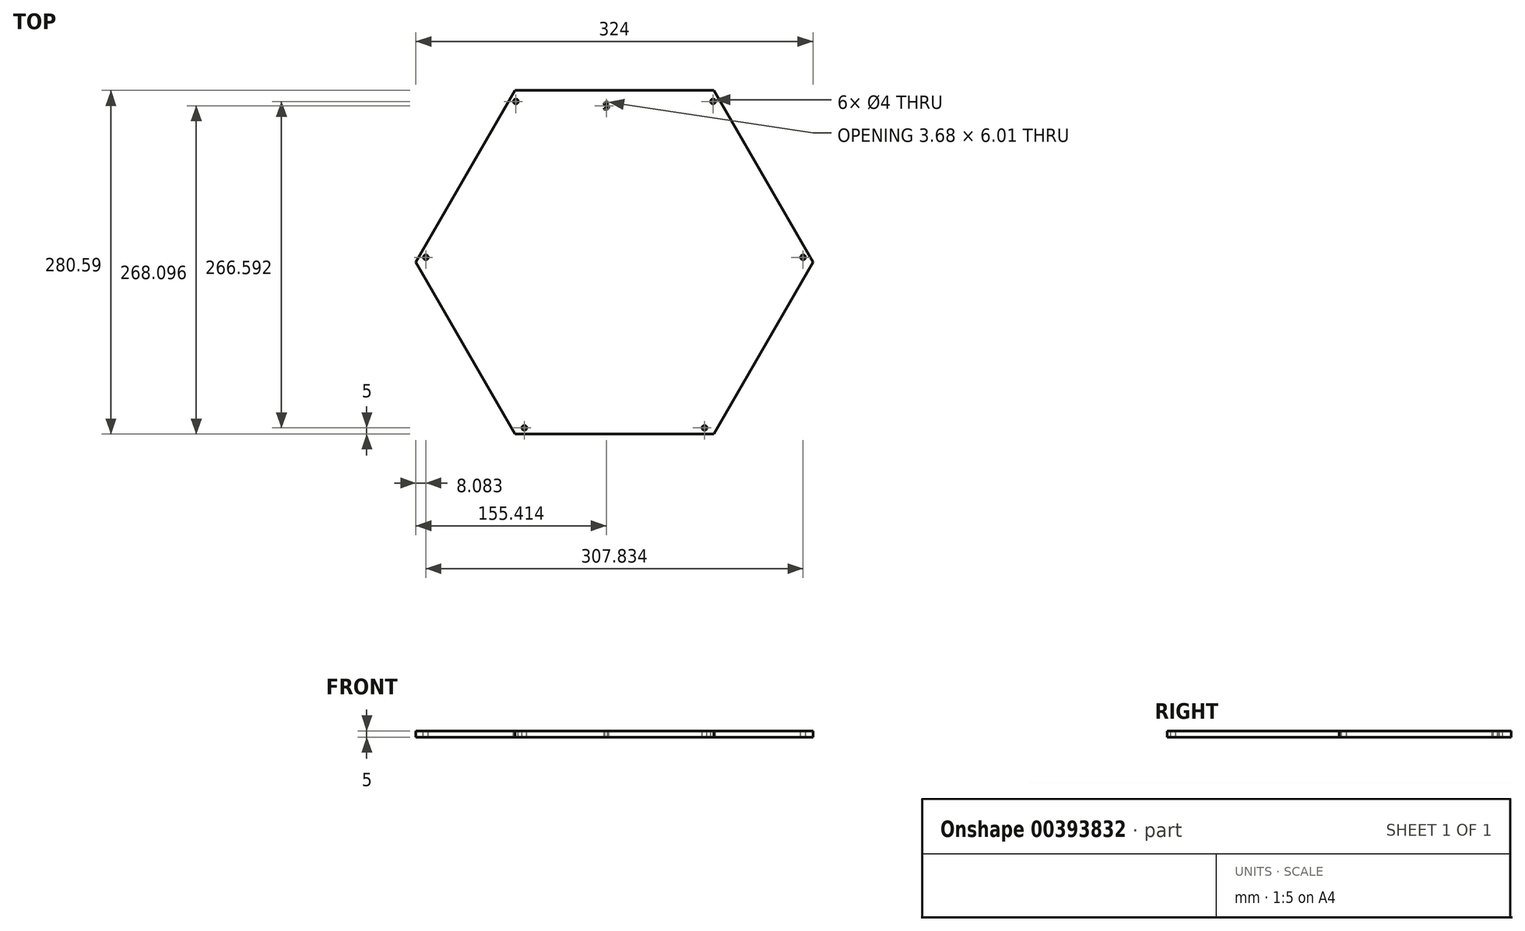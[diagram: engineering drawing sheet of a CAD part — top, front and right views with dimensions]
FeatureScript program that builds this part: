
annotation { "Feature Type Name" : "Feature", "Feature Type Description" : "" }
export const myFeature = defineFeature(function(context is Context, id is Id, definition is map)
    precondition{}
    {
        {
            var Q0;
            Q0=qCreatedBy(makeId("Top.planeOp"),FACE);
            var sketch = newSketch(context, id + "F0", { "sketchPlane" : qUnion([Q0])});
            skLineSegment(sketch, "E0", {"start": v(-81, 0) * mm, "end": v(81, 0) * mm});
            skLineSegment(sketch, "E1", {"start": v(-81, 280.6) * mm, "end": v(-162, 140.3) * mm});
            skCircle(sketch, "E2", {"center": v(0, 140.3) * mm, "radius": 140.3 * mm, "construction": true});
            skLineSegment(sketch, "E3.0", {"start": v(-81, 280.6) * mm, "end": v(81, 280.6) * mm});
            skLineSegment(sketch, "E3.2", {"start": v(162, 140.3) * mm, "end": v(81, 0) * mm});
            skLineSegment(sketch, "E3.4", {"start": v(-81, 0) * mm, "end": v(-162, 140.3) * mm});
            skPoint(sketch, "E3.0.midPoint", {"position": v(0, 280.6) * mm});
            skPoint(sketch, "E4.orphan", {"position": v(0, 420.89) * mm});
            skPoint(sketch, "E5.orphan", {"position": v(-243, 0) * mm});
            skPoint(sketch, "E6.orphan", {"position": v(243, 0) * mm});
            skLineSegment(sketch, "E7", {"start": v(81, 280.6) * mm, "end": v(162, 140.3) * mm});
            skSolve(sketch);
        }
        {
            var Q0;
            Q0=qSketchRegion(id+"F0",true);
            extrude(context, id + "F1", {"entities" : qUnion([Q0]), "depth" : 5 * mm});
        }
        {
            var Q0;
            Q0=makeQuery(id+"F1.opExtrude","CAP_FACE",FACE,{"disambiguationData":[OSD([sQuery(id+"F0.wireOp",EDGE,"E0"),sQuery(id+"F0.wireOp",EDGE,"E1"),sQuery(id+"F0.wireOp",EDGE,"E3.0"),sQuery(id+"F0.wireOp",EDGE,"E3.2"),sQuery(id+"F0.wireOp",EDGE,"E3.4"),sQuery(id+"F0.wireOp",EDGE,"E7")])],"isStart":false});
            var sketch = newSketch(context, id + "F2", { "sketchPlane" : qUnion([Q0])});
            skLineSegment(sketch, "E8.0", {"start": v(-81, 271.6) * mm, "end": v(81, 271.6) * mm});
            skLineSegment(sketch, "E9.0", {"start": v(-76.67, 278.1) * mm, "end": v(-157.67, 137.8) * mm});
            skPoint(sketch, "E10", {"position": v(-80.42, 271.6) * mm});
            skPoint(sketch, "E11.centerSnap0", {"position": v(0, 271.6) * mm});
            skCircle(sketch, "E12", {"center": v(-80.42, 271.6) * mm, "radius": 2 * mm});
            skLineSegment(sketch, "E13.0", {"start": v(-73.2, 4.5) * mm, "end": v(-154.2, 144.8) * mm});
            skLineSegment(sketch, "E14.0", {"start": v(154.2, 144.8) * mm, "end": v(73.2, 4.5) * mm});
            skLineSegment(sketch, "E15.0", {"start": v(76.67, 278.1) * mm, "end": v(157.67, 137.8) * mm});
            skPoint(sketch, "E16", {"position": v(80.42, 271.6) * mm});
            skCircle(sketch, "E17", {"center": v(80.42, 271.6) * mm, "radius": 2 * mm});
            skLineSegment(sketch, "E18.0", {"start": v(-81, 5) * mm, "end": v(81, 5) * mm});
            skPoint(sketch, "E19", {"position": v(-73.5, 5) * mm});
            skPoint(sketch, "E20", {"position": v(73.5, 5) * mm});
            skPoint(sketch, "E21", {"position": v(153.92, 144.3) * mm});
            skPoint(sketch, "E22", {"position": v(-153.92, 144.3) * mm});
            skCircle(sketch, "E23", {"center": v(-153.92, 144.3) * mm, "radius": 2 * mm});
            skCircle(sketch, "E24", {"center": v(-73.5, 5) * mm, "radius": 2 * mm});
            skCircle(sketch, "E25", {"center": v(73.5, 5) * mm, "radius": 2 * mm});
            skCircle(sketch, "E26", {"center": v(153.92, 144.3) * mm, "radius": 2 * mm});
            skSolve(sketch);
        }
        {
            var Q0;
            {var subQ0=sQuery(id+"F2.wireOp",EDGE,"E9.0");var subQ1=sQuery(id+"F2.wireOp",EDGE,"E8.0");var subQ2=makeQuery(id+"F2.imprint","INTERSECT",VERTEX,{"derivedFrom":[subQ1,subQ0]});Q0=makeQuery(id+"F2.imprint","IMPRINT",FACE,{"disambiguationData":[TD([[makeQuery(id+"F2.imprint","IMPRINT",EDGE,{"disambiguationData":[TD([[subQ2,-1.0]])],"derivedFrom":subQ1}),-1.0]])]});}
            var Q1;
            {var subQ0=sQuery(id+"F2.wireOp",EDGE,"E9.0");var subQ1=sQuery(id+"F2.wireOp",EDGE,"E8.0");var subQ2=makeQuery(id+"F2.imprint","INTERSECT",VERTEX,{"derivedFrom":[subQ1,subQ0]});Q1=makeQuery(id+"F2.imprint","IMPRINT",FACE,{"disambiguationData":[TD([[makeQuery(id+"F2.imprint","IMPRINT",EDGE,{"disambiguationData":[TD([[subQ2,-1.0]])],"derivedFrom":subQ1}),1.0]])]});}
            var Q2;
            {var subQ0=sQuery(id+"F2.wireOp",EDGE,"E9.0");var subQ1=makeQuery(id+"F2.imprint","INTERSECT",VERTEX,{"derivedFrom":[sQuery(id+"F2.wireOp",EDGE,"E8.0"),subQ0]});Q2=makeQuery(id+"F2.imprint","IMPRINT",FACE,{"disambiguationData":[TD([[makeQuery(id+"F2.imprint","IMPRINT",EDGE,{"disambiguationData":[TD([[subQ1,1.0]])],"derivedFrom":subQ0}),-1.0]])]});}
            var Q3;
            {var subQ0=sQuery(id+"F2.wireOp",EDGE,"E15.0");var subQ1=makeQuery(id+"F2.imprint","INTERSECT",VERTEX,{"derivedFrom":[sQuery(id+"F2.wireOp",EDGE,"E8.0"),subQ0]});Q3=makeQuery(id+"F2.imprint","IMPRINT",FACE,{"disambiguationData":[TD([[makeQuery(id+"F2.imprint","IMPRINT",EDGE,{"disambiguationData":[TD([[subQ1,1.0]])],"derivedFrom":subQ0}),1.0]])]});}
            var Q4;
            {var subQ0=sQuery(id+"F2.wireOp",EDGE,"E15.0");var subQ1=sQuery(id+"F2.wireOp",EDGE,"E8.0");var subQ2=makeQuery(id+"F2.imprint","INTERSECT",VERTEX,{"derivedFrom":[subQ1,subQ0]});Q4=makeQuery(id+"F2.imprint","IMPRINT",FACE,{"disambiguationData":[TD([[makeQuery(id+"F2.imprint","IMPRINT",EDGE,{"disambiguationData":[TD([[subQ2,1.0]])],"derivedFrom":subQ1}),1.0]])]});}
            var Q5;
            {var subQ0=sQuery(id+"F2.wireOp",EDGE,"E15.0");var subQ1=sQuery(id+"F2.wireOp",EDGE,"E8.0");var subQ2=makeQuery(id+"F2.imprint","INTERSECT",VERTEX,{"derivedFrom":[subQ1,subQ0]});Q5=makeQuery(id+"F2.imprint","IMPRINT",FACE,{"disambiguationData":[TD([[makeQuery(id+"F2.imprint","IMPRINT",EDGE,{"disambiguationData":[TD([[subQ2,1.0]])],"derivedFrom":subQ1}),-1.0]])]});}
            var Q6;
            {var subQ0=sQuery(id+"F2.wireOp",EDGE,"E15.0");var subQ1=makeQuery(id+"F2.imprint","INTERSECT",VERTEX,{"derivedFrom":[sQuery(id+"F2.wireOp",EDGE,"E14.0"),subQ0]});Q6=makeQuery(id+"F2.imprint","IMPRINT",FACE,{"disambiguationData":[TD([[makeQuery(id+"F2.imprint","IMPRINT",EDGE,{"disambiguationData":[TD([[subQ1,1.0]])],"derivedFrom":subQ0}),1.0]])]});}
            var Q7;
            {var subQ0=sQuery(id+"F2.wireOp",EDGE,"E15.0");var subQ1=sQuery(id+"F2.wireOp",EDGE,"E14.0");var subQ2=makeQuery(id+"F2.imprint","INTERSECT",VERTEX,{"derivedFrom":[subQ1,subQ0]});Q7=makeQuery(id+"F2.imprint","IMPRINT",FACE,{"disambiguationData":[TD([[makeQuery(id+"F2.imprint","IMPRINT",EDGE,{"disambiguationData":[TD([[subQ2,-1.0]])],"derivedFrom":subQ1}),1.0]])]});}
            var Q8;
            {var subQ0=sQuery(id+"F2.wireOp",EDGE,"E15.0");var subQ1=sQuery(id+"F2.wireOp",EDGE,"E14.0");var subQ2=makeQuery(id+"F2.imprint","INTERSECT",VERTEX,{"derivedFrom":[subQ1,subQ0]});Q8=makeQuery(id+"F2.imprint","IMPRINT",FACE,{"disambiguationData":[TD([[makeQuery(id+"F2.imprint","IMPRINT",EDGE,{"disambiguationData":[TD([[subQ2,-1.0]])],"derivedFrom":subQ1}),-1.0]])]});}
            var Q9;
            {var subQ0=sQuery(id+"F2.wireOp",EDGE,"E18.0");var subQ1=sQuery(id+"F2.wireOp",EDGE,"E14.0");var subQ2=makeQuery(id+"F2.imprint","INTERSECT",VERTEX,{"derivedFrom":[subQ1,subQ0]});Q9=makeQuery(id+"F2.imprint","IMPRINT",FACE,{"disambiguationData":[TD([[makeQuery(id+"F2.imprint","IMPRINT",EDGE,{"disambiguationData":[TD([[subQ2,1.0]])],"derivedFrom":subQ1}),-1.0]])]});}
            var Q10;
            {var subQ0=sQuery(id+"F2.wireOp",EDGE,"E18.0");var subQ1=sQuery(id+"F2.wireOp",EDGE,"E14.0");var subQ2=makeQuery(id+"F2.imprint","INTERSECT",VERTEX,{"derivedFrom":[subQ1,subQ0]});Q10=makeQuery(id+"F2.imprint","IMPRINT",FACE,{"disambiguationData":[TD([[makeQuery(id+"F2.imprint","IMPRINT",EDGE,{"disambiguationData":[TD([[subQ2,1.0]])],"derivedFrom":subQ1}),1.0]])]});}
            var Q11;
            {var subQ0=sQuery(id+"F2.wireOp",EDGE,"E18.0");var subQ1=makeQuery(id+"F2.imprint","INTERSECT",VERTEX,{"derivedFrom":[sQuery(id+"F2.wireOp",EDGE,"E14.0"),subQ0]});Q11=makeQuery(id+"F2.imprint","IMPRINT",FACE,{"disambiguationData":[TD([[makeQuery(id+"F2.imprint","IMPRINT",EDGE,{"disambiguationData":[TD([[subQ1,1.0]])],"derivedFrom":subQ0}),-1.0]])]});}
            var Q12;
            {var subQ0=sQuery(id+"F2.wireOp",EDGE,"E18.0");var subQ1=sQuery(id+"F2.wireOp",EDGE,"E13.0");var subQ2=makeQuery(id+"F2.imprint","INTERSECT",VERTEX,{"derivedFrom":[subQ1,subQ0]});Q12=makeQuery(id+"F2.imprint","IMPRINT",FACE,{"disambiguationData":[TD([[makeQuery(id+"F2.imprint","IMPRINT",EDGE,{"disambiguationData":[TD([[subQ2,-1.0]])],"derivedFrom":subQ1}),-1.0]])]});}
            var Q13;
            {var subQ0=sQuery(id+"F2.wireOp",EDGE,"E18.0");var subQ1=sQuery(id+"F2.wireOp",EDGE,"E13.0");var subQ2=makeQuery(id+"F2.imprint","INTERSECT",VERTEX,{"derivedFrom":[subQ1,subQ0]});Q13=makeQuery(id+"F2.imprint","IMPRINT",FACE,{"disambiguationData":[TD([[makeQuery(id+"F2.imprint","IMPRINT",EDGE,{"disambiguationData":[TD([[subQ2,-1.0]])],"derivedFrom":subQ1}),1.0]])]});}
            var Q14;
            {var subQ0=sQuery(id+"F2.wireOp",EDGE,"E18.0");var subQ1=makeQuery(id+"F2.imprint","INTERSECT",VERTEX,{"derivedFrom":[sQuery(id+"F2.wireOp",EDGE,"E13.0"),subQ0]});Q14=makeQuery(id+"F2.imprint","IMPRINT",FACE,{"disambiguationData":[TD([[makeQuery(id+"F2.imprint","IMPRINT",EDGE,{"disambiguationData":[TD([[subQ1,1.0]])],"derivedFrom":subQ0}),-1.0]])]});}
            var Q15;
            {var subQ0=sQuery(id+"F2.wireOp",EDGE,"E13.0");var subQ1=sQuery(id+"F2.wireOp",EDGE,"E9.0");var subQ2=makeQuery(id+"F2.imprint","INTERSECT",VERTEX,{"derivedFrom":[subQ1,subQ0]});Q15=makeQuery(id+"F2.imprint","IMPRINT",FACE,{"disambiguationData":[TD([[makeQuery(id+"F2.imprint","IMPRINT",EDGE,{"disambiguationData":[TD([[subQ2,1.0]])],"derivedFrom":subQ1}),1.0]])]});}
            var Q16;
            {var subQ0=sQuery(id+"F2.wireOp",EDGE,"E9.0");var subQ1=makeQuery(id+"F2.imprint","INTERSECT",VERTEX,{"derivedFrom":[subQ0,sQuery(id+"F2.wireOp",EDGE,"E13.0")]});Q16=makeQuery(id+"F2.imprint","IMPRINT",FACE,{"disambiguationData":[TD([[makeQuery(id+"F2.imprint","IMPRINT",EDGE,{"disambiguationData":[TD([[subQ1,1.0]])],"derivedFrom":subQ0}),-1.0]])]});}
            var Q17;
            {var subQ0=sQuery(id+"F2.wireOp",EDGE,"E13.0");var subQ1=sQuery(id+"F2.wireOp",EDGE,"E9.0");var subQ2=makeQuery(id+"F2.imprint","INTERSECT",VERTEX,{"derivedFrom":[subQ1,subQ0]});Q17=makeQuery(id+"F2.imprint","IMPRINT",FACE,{"disambiguationData":[TD([[makeQuery(id+"F2.imprint","IMPRINT",EDGE,{"disambiguationData":[TD([[subQ2,-1.0]])],"derivedFrom":subQ1}),1.0]])]});}
            extrude(context, id + "F3", {"entities" : qUnion([Q0, Q1, Q2, Q3, Q4, Q5, Q6, Q7, Q8, Q9, Q10, Q11, Q12, Q13, Q14, Q15, Q16, Q17]), "operationType" : NewBodyOperationType.REMOVE, "oppositeDirection" : true, "depth" : 25 * mm});
        }
        {
            var Q0;
            Q0=makeQuery(id+"F1.opExtrude","CAP_FACE",FACE,{"disambiguationData":[OSD([sQuery(id+"F0.wireOp",EDGE,"E0"),sQuery(id+"F0.wireOp",EDGE,"E1"),sQuery(id+"F0.wireOp",EDGE,"E3.0"),sQuery(id+"F0.wireOp",EDGE,"E3.2"),sQuery(id+"F0.wireOp",EDGE,"E3.4"),sQuery(id+"F0.wireOp",EDGE,"E7")])],"isStart":false});
            var sketch = newSketch(context, id + "F4", { "sketchPlane" : qUnion([Q0])});
            skText(sketch, "E27", { "text": "S", "fontName": "OpenSans-Regular.ttf"});
            const initialGuessF4  = {"E27": [-0.00885, 0.26517, 1, 0, 0.0059]};
            skSetInitialGuess(sketch, initialGuessF4);
            skSolve(sketch);
        }
        {
            var Q0;
            Q0=makeQuery(id+"F4.imprint","IMPRINT",FACE,{"disambiguationData":[TD([[makeQuery(id+"F4.imprint","IMPRINT",EDGE,{"derivedFrom":sQuery(id+"F4.wireOp",EDGE,"E27.sketch_text.stroke-0")}),-1.0]])]});
            extrude(context, id + "F5", {"entities" : qUnion([Q0]), "operationType" : NewBodyOperationType.REMOVE, "oppositeDirection" : true, "depth" : 25 * mm});
        }
    });
